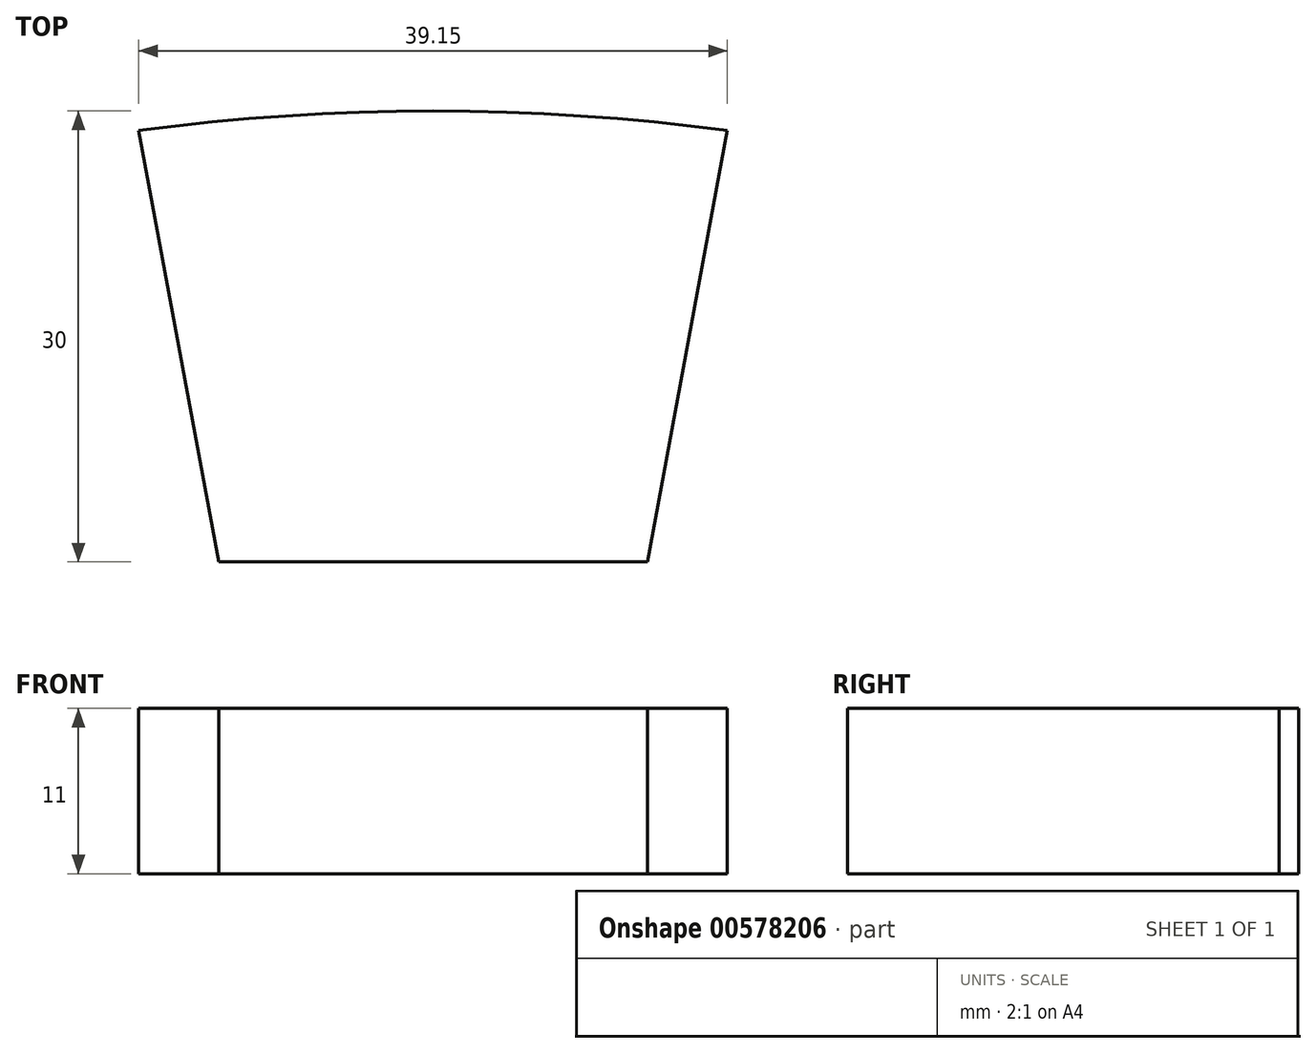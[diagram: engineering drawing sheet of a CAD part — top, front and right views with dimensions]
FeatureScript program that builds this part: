
annotation { "Feature Type Name" : "Feature", "Feature Type Description" : "" }
export const myFeature = defineFeature(function(context is Context, id is Id, definition is map)
    precondition{}
    {
        {
            var Q0;
            Q0=qCreatedBy(makeId("Top.planeOp"),FACE);
            var sketch = newSketch(context, id + "F0", { "sketchPlane" : qUnion([Q0])});
            skLineSegment(sketch, "E0.bottom", {"start": v(14.26, -15) * mm, "end": v(-14.26, -15) * mm});
            skPoint(sketch, "E0.middle", {"position": v(0, 0) * mm});
            skArc(sketch, "E1", {"start": v(19.57, 13.7) * mm, "mid": v(0, 15) * mm, "end": v(-19.57, 13.7) * mm});
            skLineSegment(sketch, "E2", {"start": v(-19.57, 13.7) * mm, "end": v(-14.26, -15) * mm});
            skLineSegment(sketch, "E3", {"start": v(19.58, 13.7) * mm, "end": v(14.26, -15) * mm});
            skPoint(sketch, "E4.orphan", {"position": v(-19.57, -15) * mm});
            skPoint(sketch, "E5.orphan", {"position": v(19.58, -15) * mm});
            skPoint(sketch, "E0.right.end.orphan", {"position": v(-19.57, 15) * mm});
            skPoint(sketch, "E0.left.end.orphan", {"position": v(19.57, 15) * mm});
            skSolve(sketch);
        }
        {
            var Q0;
            Q0=qSketchRegion(id+"F0",true);
            extrude(context, id + "F1", {"entities" : qUnion([Q0]), "depth" : 11 * mm, "offsetDistance" : 25 * mm});
        }
    });
